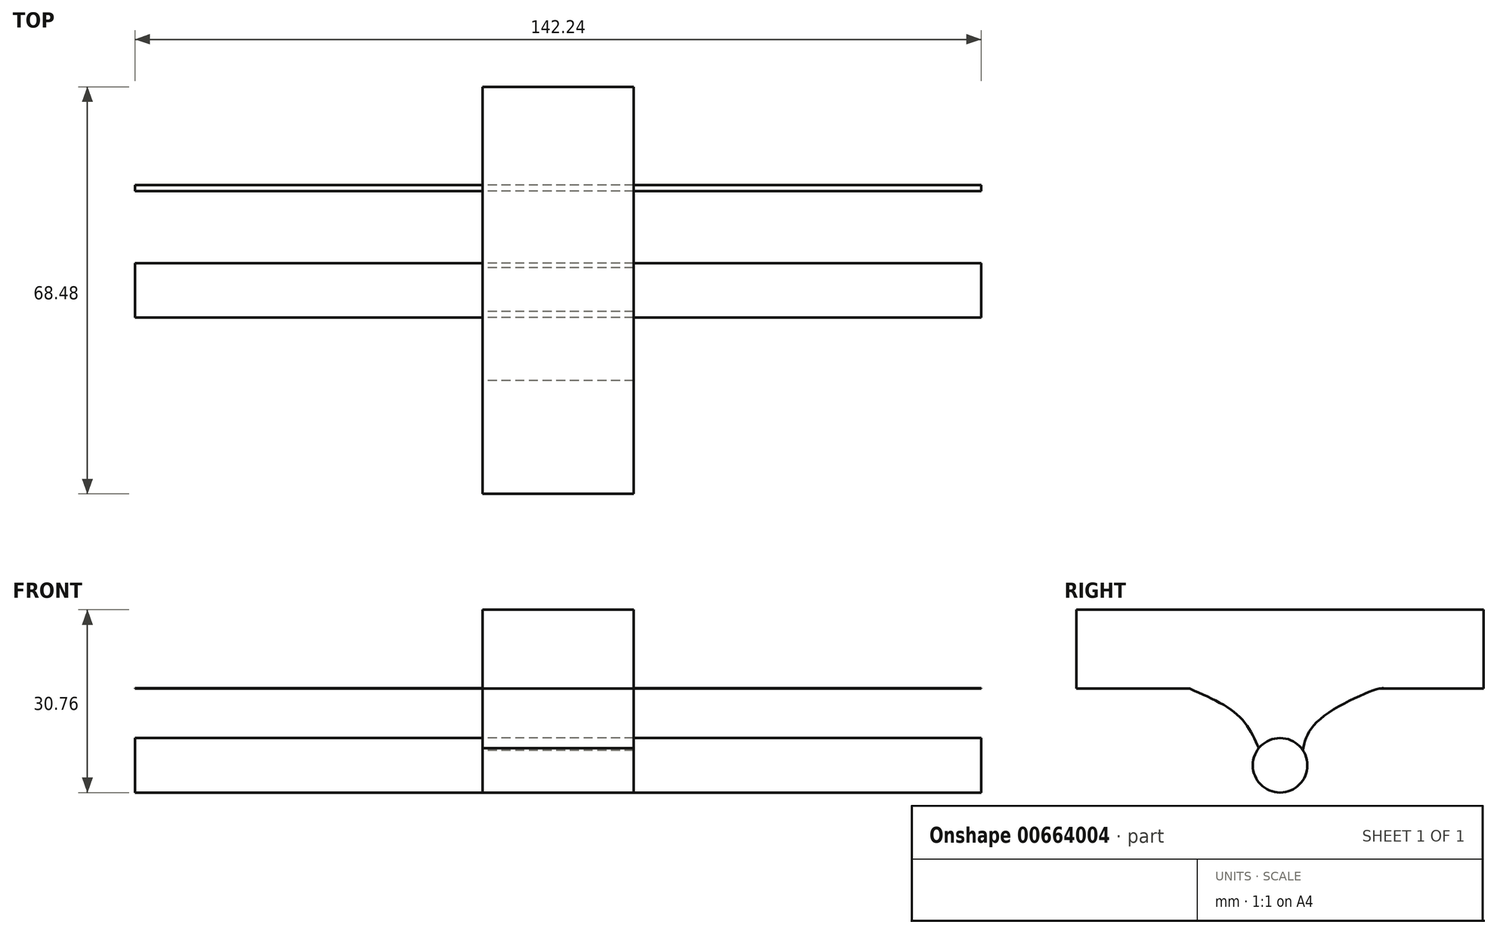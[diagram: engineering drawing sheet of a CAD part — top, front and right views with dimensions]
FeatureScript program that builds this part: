
annotation { "Feature Type Name" : "Feature", "Feature Type Description" : "" }
export const myFeature = defineFeature(function(context is Context, id is Id, definition is map)
    precondition{}
    {
        {
            var Q0;
            Q0=qCreatedBy(makeId("Right.planeOp"),FACE);
            var sketch = newSketch(context, id + "F0", { "sketchPlane" : qUnion([Q0])});
            skCircle(sketch, "E0", {"center": v(0, -12.88) * mm, "radius": 4.58 * mm});
            skFitSpline(sketch, "E1", {"points": [v(-3.58, -10.02) * mm, v(-6.9, -4.64) * mm, v(-15.17, 0) * mm], "startDerivative": vector(-5.64, 12.74) * mm, "endDerivative": vector(-17.13, 7.45) * mm});
            skFitSpline(sketch, "E2", {"points": [v(3.83, -10.37) * mm, v(6.4, -5.4) * mm, v(16.68, 0) * mm, v(17.68, 0) * mm], "startDerivative": vector(2.7, 13.94) * mm, "endDerivative": vector(4.5, -1.24) * mm});
            skLineSegment(sketch, "E3.bottom", {"start": v(34.24, 0) * mm, "end": v(-34.24, 0) * mm});
            skLineSegment(sketch, "E3.top", {"start": v(34.24, 13.3) * mm, "end": v(-34.24, 13.3) * mm});
            skLineSegment(sketch, "E3.left", {"start": v(34.24, 0) * mm, "end": v(34.24, 13.3) * mm});
            skLineSegment(sketch, "E3.right", {"start": v(-34.24, 0) * mm, "end": v(-34.24, 13.3) * mm});
            skPoint(sketch, "E3.middle", {"position": v(0, 6.65) * mm});
            skSolve(sketch);
        }
        {
            var Q0;
            {var subQ0=sQuery(id+"F0.wireOp",EDGE,"E0");var subQ1=makeQuery(id+"F0.imprint","INTERSECT",VERTEX,{"derivedFrom":[subQ0,sQuery(id+"F0.wireOp",EDGE,"E1")]});Q0=makeQuery(id+"F0.imprint","IMPRINT",FACE,{"disambiguationData":[TD([[makeQuery(id+"F0.imprint","IMPRINT",EDGE,{"disambiguationData":[TD([[subQ1,1.0]])],"derivedFrom":subQ0}),1.0]])]});}
            var Q1;
            {var subQ0=sQuery(id+"F0.wireOp",EDGE,"E3.bottom");var subQ1=sQuery(id+"F0.wireOp",EDGE,"E2");var subQ2=makeQuery(id+"F0.imprint","INTERSECT",VERTEX,{"disambiguationData":[OD(0.0)],"derivedFrom":[subQ1,subQ0]});Q1=makeQuery(id+"F0.imprint","IMPRINT",FACE,{"disambiguationData":[TD([[makeQuery(id+"F0.imprint","IMPRINT",EDGE,{"disambiguationData":[TD([[subQ2,1.0]])],"derivedFrom":subQ1}),-1.0]])]});}
            extrude(context, id + "F1", {"entities" : qUnion([Q0, Q1]), "endBound" : BoundingType.SYMMETRIC, "depth" : 142.24 * mm, "offsetDistance" : 25.4 * mm});
        }
        {
            var Q0;
            Q0 = qSketchRegion(id + "F0", true);
            extrude(context, id + "F2", {"entities" : qUnion([Q0]), "endBound" : BoundingType.SYMMETRIC, "depth" : 25.4 * mm, "offsetDistance" : 25.4 * mm});
        }
    });
